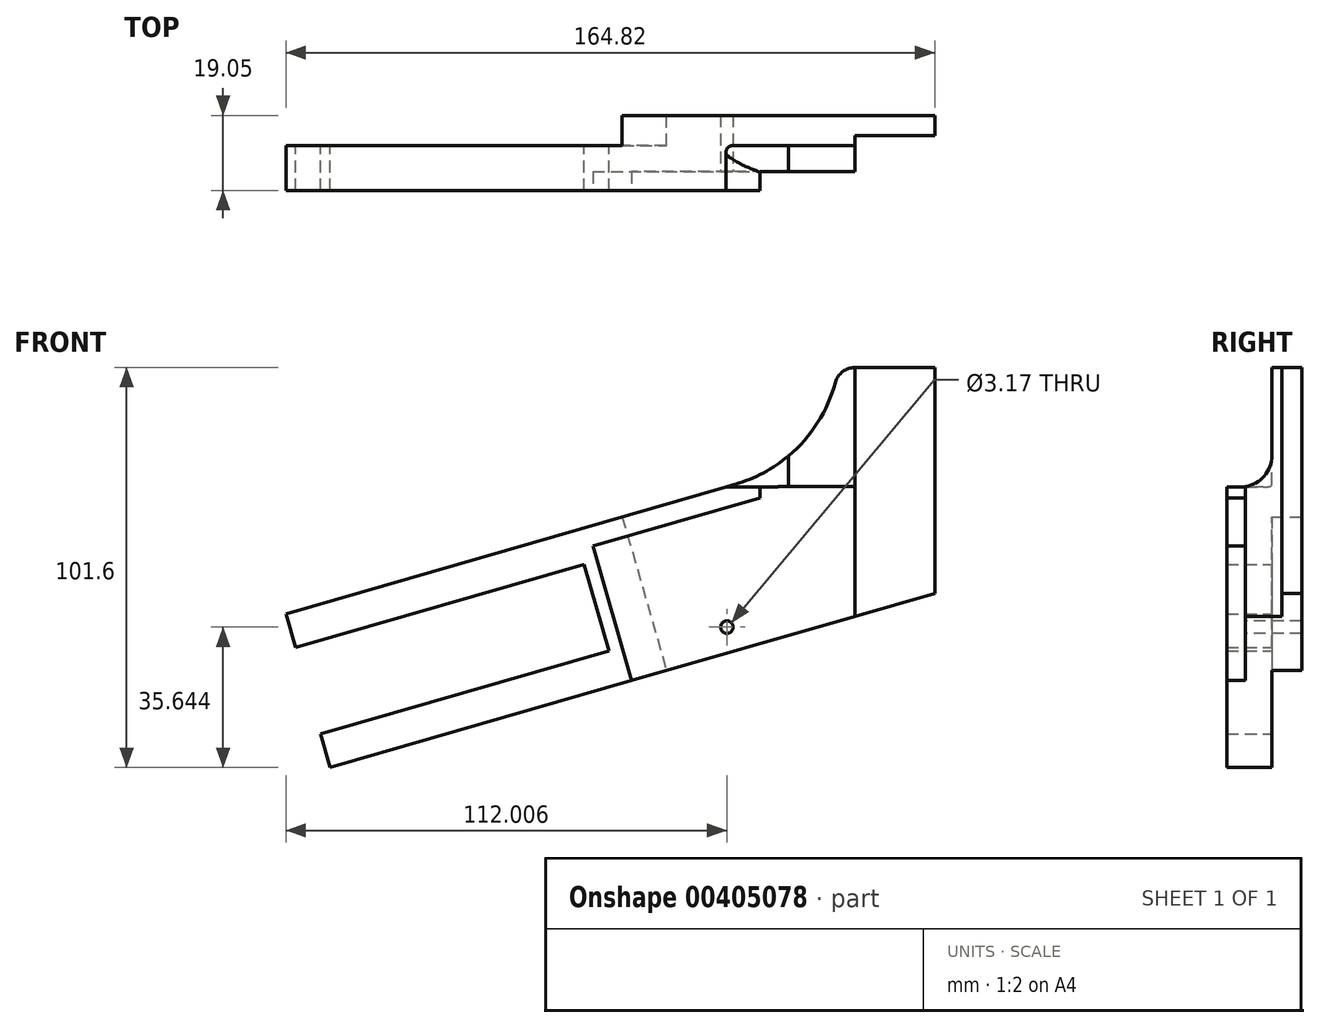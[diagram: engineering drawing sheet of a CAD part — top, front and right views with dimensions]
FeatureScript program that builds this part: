
annotation { "Feature Type Name" : "Feature", "Feature Type Description" : "" }
export const myFeature = defineFeature(function(context is Context, id is Id, definition is map)
    precondition{}
    {
        {
            var Q0;
            Q0=qCreatedBy(makeId("Front.planeOp"),FACE);
            var sketch = newSketch(context, id + "F0", { "sketchPlane" : qUnion([Q0])});
            skLineSegment(sketch, "E0.bottom", {"start": v(0, 0) * mm, "end": v(-50.8, 0) * mm});
            skLineSegment(sketch, "E0.top", {"start": v(0, -55.88) * mm, "end": v(-25.4, -55.88) * mm});
            skLineSegment(sketch, "E0.left", {"start": v(0, 0) * mm, "end": v(0, -55.88) * mm});
            skArc(sketch, "E1", {"start": v(-50.8, 0) * mm, "mid": v(-53.89, -1.05) * mm, "end": v(-55.7, -3.75) * mm});
            skLineSegment(sketch, "E2", {"start": v(-25.4, -55.88) * mm, "end": v(-184.04, -101.6) * mm});
            skLineSegment(sketch, "E3", {"start": v(-184.04, -101.6) * mm, "end": v(-186.5, -93.06) * mm});
            skLineSegment(sketch, "E4", {"start": v(-195.3, -62.55) * mm, "end": v(-81.19, -29.66) * mm});
            skArc(sketch, "E5", {"start": v(-81.19, -29.66) * mm, "mid": v(-65.05, -20.05) * mm, "end": v(-55.7, -3.75) * mm});
            skLineSegment(sketch, "E6", {"start": v(-192.84, -71.1) * mm, "end": v(-119.62, -50) * mm});
            skLineSegment(sketch, "E7", {"start": v(-119.62, -50) * mm, "end": v(-113.29, -71.96) * mm});
            skLineSegment(sketch, "E8", {"start": v(-113.29, -71.96) * mm, "end": v(-186.5, -93.06) * mm});
            skLineSegment(sketch, "E9.trimOffspring", {"start": v(-192.84, -71.1) * mm, "end": v(-195.3, -62.55) * mm});
            skLineSegment(sketch, "E10.bottom", {"start": v(-50.8, 0) * mm, "end": v(-30.48, 0) * mm});
            skLineSegment(sketch, "E10.left", {"start": v(-50.8, 0) * mm, "end": v(-50.8, -63.2) * mm});
            skLineSegment(sketch, "E10.right", {"start": v(-30.48, 0) * mm, "end": v(-30.48, -57.34) * mm});
            skSolve(sketch);
        }
        {
            var Q0;
            Q0=makeQuery(id+"F0.imprint","IMPRINT",FACE,{"disambiguationData":[TD([[makeQuery(id+"F0.imprint","IMPRINT",EDGE,{"derivedFrom":sQuery(id+"F0.wireOp",EDGE,"E0.bottom")}),1.0]])]});
            var Q1;
            Q1=makeQuery(id+"F0.imprint","IMPRINT",FACE,{"disambiguationData":[TD([[makeQuery(id+"F0.imprint","IMPRINT",EDGE,{"derivedFrom":sQuery(id+"F0.wireOp",EDGE,"E1")}),1.0]])]});
            var Q2;
            Q2=makeQuery(id+"F0.imprint","IMPRINT",FACE,{"disambiguationData":[TD([[makeQuery(id+"F0.imprint","IMPRINT",EDGE,{"derivedFrom":sQuery(id+"F0.wireOp",EDGE,"E10.bottom")}),-1.0]])]});
            extrude(context, id + "F1", {"entities" : qUnion([Q0, Q1, Q2]), "depth" : 19.05 * mm});
        }
        {
            var Q0;
            Q0=makeQuery(id+"F1.opExtrude","CAP_FACE",FACE,{"disambiguationData":[OSD([sQuery(id+"F0.wireOp",EDGE,"E0.bottom"),sQuery(id+"F0.wireOp",EDGE,"E0.top"),sQuery(id+"F0.wireOp",EDGE,"E0.left"),sQuery(id+"F0.wireOp",EDGE,"E1"),sQuery(id+"F0.wireOp",EDGE,"E2"),sQuery(id+"F0.wireOp",EDGE,"E3"),sQuery(id+"F0.wireOp",EDGE,"E4"),sQuery(id+"F0.wireOp",EDGE,"E5"),sQuery(id+"F0.wireOp",EDGE,"E6"),sQuery(id+"F0.wireOp",EDGE,"E7"),sQuery(id+"F0.wireOp",EDGE,"E8"),sQuery(id+"F0.wireOp",EDGE,"E9.trimOffspring"),sQuery(id+"F0.wireOp",EDGE,"E10.bottom")])],"isStart":false});
            var sketch = newSketch(context, id + "F2", { "sketchPlane" : qUnion([Q0])});
            skLineSegment(sketch, "E11.bottom", {"start": v(-50.8, 0) * mm, "end": v(-30.48, 0) * mm});
            skLineSegment(sketch, "E11.left", {"start": v(-50.8, 0) * mm, "end": v(-50.8, -63.2) * mm});
            skLineSegment(sketch, "E11.right", {"start": v(-30.48, 0) * mm, "end": v(-30.48, -57.34) * mm});
            skLineSegment(sketch, "E12", {"start": v(-30.48, -57.34) * mm, "end": v(-50.8, -63.2) * mm});
            skSolve(sketch);
        }
        {
            var Q0;
            Q0 = qSketchRegion(id + "F2", true);
            extrude(context, id + "F3", {"entities" : qUnion([Q0]), "operationType" : NewBodyOperationType.REMOVE, "oppositeDirection" : true, "depth" : 13.97 * mm});
        }
        {
            var Q0;
            Q0=makeQuery(id+"F0.imprint","IMPRINT",FACE,{"disambiguationData":[TD([[makeQuery(id+"F0.imprint","IMPRINT",EDGE,{"derivedFrom":sQuery(id+"F0.wireOp",EDGE,"E1")}),1.0]])]});
            var sketch = newSketch(context, id + "F4", { "sketchPlane" : qUnion([Q0])});
            skPoint(sketch, "E13", {"position": v(-195.3, -62.55) * mm});
            skPoint(sketch, "E14", {"position": v(-184.04, -101.6) * mm});
            skLineSegment(sketch, "E15", {"start": v(-195.3, -62.55) * mm, "end": v(-184.04, -101.6) * mm});
            skLineSegment(sketch, "E16", {"start": v(-184.04, -101.6) * mm, "end": v(-98.62, -76.98) * mm});
            skLineSegment(sketch, "E17", {"start": v(-195.3, -62.55) * mm, "end": v(-109.87, -37.93) * mm});
            skLineSegment(sketch, "E18", {"start": v(-109.87, -37.93) * mm, "end": v(-98.62, -76.98) * mm});
            skSolve(sketch);
        }
        {
            var Q0;
            Q0 = qSketchRegion(id + "F4", true);
            extrude(context, id + "F5", {"entities" : qUnion([Q0]), "operationType" : NewBodyOperationType.REMOVE, "depth" : 7.62 * mm});
        }
        {
            var Q0;
            {var subQ0=sQuery(id+"F0.wireOp",EDGE,"E2");var subQ1=sQuery(id+"F0.wireOp",EDGE,"E0.left");var subQ2=sQuery(id+"F0.wireOp",EDGE,"E0.top");var subQ3=sQuery(id+"F0.wireOp",EDGE,"E10.bottom");var subQ4=sQuery(id+"F0.wireOp",EDGE,"E0.bottom");Q0=makeQuery(id+"F3.boolean.opBoolean","SPLIT",FACE,{"disambiguationData":[TD([makeQuery(id+"F1.opExtrude","SWEPT_FACE",FACE,{"disambiguationData":[OSD([subQ2])]})])],"derivedFrom":makeQuery(id+"F1.opExtrude","CAP_FACE",FACE,{"disambiguationData":[OSD([subQ4,subQ2,subQ1,sQuery(id+"F0.wireOp",EDGE,"E1"),subQ0,sQuery(id+"F0.wireOp",EDGE,"E3"),sQuery(id+"F0.wireOp",EDGE,"E4"),sQuery(id+"F0.wireOp",EDGE,"E5"),sQuery(id+"F0.wireOp",EDGE,"E6"),sQuery(id+"F0.wireOp",EDGE,"E7"),sQuery(id+"F0.wireOp",EDGE,"E8"),sQuery(id+"F0.wireOp",EDGE,"E9.trimOffspring"),subQ3])],"isStart":false})});}
            var sketch = newSketch(context, id + "F6", { "sketchPlane" : qUnion([Q0])});
            skCircle(sketch, "E19", {"center": v(-6.35, -6.35) * mm, "radius": 3.18 * mm});
            skCircle(sketch, "E20", {"center": v(-24.13, -6.35) * mm, "radius": 3.18 * mm});
            skLineSegment(sketch, "E21", {"start": v(13.25, -21.59) * mm, "end": v(-85.18, -21.6) * mm, "construction": true});
            skPoint(sketch, "E22", {"position": v(-50.8, 0) * mm});
            skLineSegment(sketch, "E23", {"start": v(-50.8, -30.35) * mm, "end": v(-101.6, -30.35) * mm});
            skLineSegment(sketch, "E24", {"start": v(-50.8, 0) * mm, "end": v(-50.8, -30.35) * mm});
            skArc(sketch, "E25", {"start": v(-50.8, 0) * mm, "mid": v(-53.89, -1.05) * mm, "end": v(-55.7, -3.75) * mm});
            skArc(sketch, "E26", {"start": v(-101.6, -29.7) * mm, "mid": v(-73.23, -26.32) * mm, "end": v(-55.7, -3.75) * mm});
            skLineSegment(sketch, "E27", {"start": v(-101.6, -30.35) * mm, "end": v(-101.6, -29.7) * mm});
            skLineSegment(sketch, "E28", {"start": v(-30.48, -10.41) * mm, "end": v(-30.48, -32.77) * mm});
            skLineSegment(sketch, "E29", {"start": v(-30.48, -10.41) * mm, "end": v(-28.9, -10.41) * mm});
            skLineSegment(sketch, "E30", {"start": v(-28.9, -10.41) * mm, "end": v(-28.9, -32.77) * mm});
            skLineSegment(sketch, "E31", {"start": v(-28.9, -32.77) * mm, "end": v(-30.48, -32.77) * mm});
            skLineSegment(sketch, "E32", {"start": v(-28.9, -12.32) * mm, "end": v(-7.97, -12.32) * mm});
            skSolve(sketch);
        }
        {
            var Q0;
            {var subQ0=sQuery(id+"F6.wireOp",EDGE,"E24");Q0=makeQuery(id+"F6.imprint","IMPRINT",FACE,{"disambiguationData":[TD([[makeQuery(id+"F6.imprint","IMPRINT",EDGE,{"derivedFrom":subQ0}),-1.0]])]});}
            extrude(context, id + "F7", {"entities" : qUnion([Q0]), "operationType" : NewBodyOperationType.REMOVE, "oppositeDirection" : true, "depth" : 11.43 * mm});
        }
        {
            var Q0;
            Q0=makeQuery(id+"F7.boolean.opBoolean","COPY",EDGE,{"derivedFrom":makeQuery(id+"F7.opExtrude","CAP_EDGE",EDGE,{"disambiguationData":[OSD([sQuery(id+"F6.wireOp",EDGE,"E23")])],"isStart":false})});
            fillet(context, id + "F8", {"entities" : qUnion([Q0]), "radius" : 7.94 * mm, "tangentPropagation" : true, "allowEdgeOverflow" : false});
        }
        {
            var Q0;
            {var subQ0=sQuery(id+"F0.wireOp",EDGE,"E4");var subQ1=sQuery(id+"F0.wireOp",EDGE,"E3");var subQ2=sQuery(id+"F0.wireOp",EDGE,"E2");var subQ3=sQuery(id+"F0.wireOp",EDGE,"E1");var subQ4=sQuery(id+"F0.wireOp",EDGE,"E5");var subQ5=sQuery(id+"F0.wireOp",EDGE,"E6");var subQ6=sQuery(id+"F0.wireOp",EDGE,"E7");var subQ7=sQuery(id+"F0.wireOp",EDGE,"E8");var subQ8=sQuery(id+"F0.wireOp",EDGE,"E9.trimOffspring");Q0=makeQuery(id+"F3.boolean.opBoolean","SPLIT",FACE,{"disambiguationData":[TD([makeQuery(id+"F1.opExtrude","SWEPT_FACE",FACE,{"disambiguationData":[OSD([subQ3])]})])],"derivedFrom":makeQuery(id+"F1.opExtrude","CAP_FACE",FACE,{"disambiguationData":[OSD([sQuery(id+"F0.wireOp",EDGE,"E0.bottom"),sQuery(id+"F0.wireOp",EDGE,"E0.top"),sQuery(id+"F0.wireOp",EDGE,"E0.left"),subQ3,subQ2,subQ1,subQ0,subQ4,subQ5,subQ6,subQ7,subQ8,sQuery(id+"F0.wireOp",EDGE,"E10.bottom")])],"isStart":false})});}
            var sketch = newSketch(context, id + "F9", { "sketchPlane" : qUnion([Q0])});
            skLineSegment(sketch, "E33", {"start": v(22.55, -19.05) * mm, "end": v(-137.17, -19.05) * mm, "construction": true});
            skLineSegment(sketch, "E34", {"start": v(-216.65, -89.85) * mm, "end": v(44.78, -14.5) * mm, "construction": true});
            skLineSegment(sketch, "E35", {"start": v(-40.64, 0) * mm, "end": v(-40.64, -73.86) * mm, "construction": true});
            skCircle(sketch, "E36", {"center": v(-40.64, -50.8) * mm, "radius": 38.1 * mm});
            skCircle(sketch, "E37", {"center": v(-40.64, -50.8) * mm, "radius": 4.76 * mm});
            skCircle(sketch, "E38", {"center": v(-40.64, -50.8) * mm, "radius": 3.18 * mm});
            skLineSegment(sketch, "E39.top", {"start": v(-53.98, -22.23) * mm, "end": v(-53.98, -22.23) * mm});
            skCircle(sketch, "E40", {"center": v(-73.37, -44.45) * mm, "radius": 4.76 * mm});
            skLineSegment(sketch, "E41", {"start": v(-74.91, -49) * mm, "end": v(-41.55, -55.48) * mm});
            skLineSegment(sketch, "E42", {"start": v(-53.98, -22.23) * mm, "end": v(-53.98, -14.4) * mm});
            skLineSegment(sketch, "E43", {"start": v(-53.98, -14.4) * mm, "end": v(-68.58, -3.18) * mm});
            skLineSegment(sketch, "E44", {"start": v(-68.58, -3.18) * mm, "end": v(-60.07, -18.02) * mm});
            skCircle(sketch, "E45", {"center": v(-40.64, -30.4) * mm, "radius": 15.64 * mm});
            skLineSegment(sketch, "E46", {"start": v(-94.35, -75.75) * mm, "end": v(-78.48, -71.18) * mm});
            skLineSegment(sketch, "E47", {"start": v(-78.48, -71.18) * mm, "end": v(-81.12, -62.03) * mm});
            skLineSegment(sketch, "E48", {"start": v(-81.12, -62.03) * mm, "end": v(-96.99, -66.6) * mm});
            skLineSegment(sketch, "E49", {"start": v(-96.99, -66.6) * mm, "end": v(-94.35, -75.75) * mm});
            skLineSegment(sketch, "E50", {"start": v(-86.42, -73.46) * mm, "end": v(-80.09, -95.43) * mm});
            skLineSegment(sketch, "E51", {"start": v(-80.09, -95.43) * mm, "end": v(-94.35, -75.75) * mm});
            skCircle(sketch, "E52", {"center": v(-83.3, -65.96) * mm, "radius": 1.59 * mm});
            skLineSegment(sketch, "E53", {"start": v(-65.92, -60.95) * mm, "end": v(-107.75, -73) * mm, "construction": true});
            skPoint(sketch, "E54", {"position": v(-195.3, -62.55) * mm});
            skPoint(sketch, "E55", {"position": v(-192.84, -71.1) * mm});
            skCircle(sketch, "E56", {"center": v(-93.06, -68.77) * mm, "radius": 1.59 * mm});
            skLineSegment(sketch, "E57", {"start": v(-78.13, -19.05) * mm, "end": v(-78.13, -106.08) * mm, "construction": true});
            skLineSegment(sketch, "E58", {"start": v(-117.33, -45.37) * mm, "end": v(-84.15, -35.8) * mm});
            skLineSegment(sketch, "E59", {"start": v(-84.15, -35.8) * mm, "end": v(-61.15, -29.18) * mm});
            skLineSegment(sketch, "E60", {"start": v(-117.33, -45.37) * mm, "end": v(-107.48, -79.54) * mm});
            skLineSegment(sketch, "E61", {"start": v(-107.48, -79.54) * mm, "end": v(-50.8, -63.2) * mm});
            skLineSegment(sketch, "E62", {"start": v(-74.93, -33.15) * mm, "end": v(-74.93, -28.4) * mm});
            skLineSegment(sketch, "E63", {"start": v(-74.93, -28.4) * mm, "end": v(-49.66, -28.4) * mm});
            skLineSegment(sketch, "E64", {"start": v(-50.8, -63.2) * mm, "end": v(-50.8, -28.4) * mm});
            skSolve(sketch);
        }
        {
            var Q0;
            {var subQ6=sQuery(id+"F9.wireOp",EDGE,"E47");Q0=makeQuery(id+"F9.imprint","IMPRINT",FACE,{"disambiguationData":[TD([[makeQuery(id+"F9.imprint","IMPRINT",EDGE,{"derivedFrom":subQ6}),-1.0]])]});}
            var Q1;
            {var subQ1=sQuery(id+"F9.wireOp",EDGE,"E47");Q1=makeQuery(id+"F9.imprint","IMPRINT",FACE,{"disambiguationData":[TD([[makeQuery(id+"F9.imprint","IMPRINT",EDGE,{"derivedFrom":subQ1}),1.0]])]});}
            var Q2;
            Q2=makeQuery(id+"F9.imprint","IMPRINT",FACE,{"disambiguationData":[TD([[makeQuery(id+"F9.imprint","IMPRINT",EDGE,{"derivedFrom":sQuery(id+"F9.wireOp",EDGE,"E52")}),1.0]])]});
            var Q3;
            Q3=makeQuery(id+"F9.imprint","IMPRINT",FACE,{"disambiguationData":[TD([[makeQuery(id+"F9.imprint","IMPRINT",EDGE,{"derivedFrom":sQuery(id+"F9.wireOp",EDGE,"E56")}),1.0]])]});
            var Q4;
            {var subQ1=sQuery(id+"F9.wireOp",EDGE,"E61");var subQ3=sQuery(id+"F9.wireOp",EDGE,"E36");var subQ4=makeQuery(id+"F9.imprint","INTERSECT",VERTEX,{"derivedFrom":[subQ3,subQ1]});Q4=makeQuery(id+"F9.imprint","IMPRINT",FACE,{"disambiguationData":[TD([[makeQuery(id+"F9.imprint","IMPRINT",EDGE,{"disambiguationData":[TD([[subQ4,1.0]])],"derivedFrom":subQ3}),1.0]])]});}
            var Q5;
            {var subQ5=sQuery(id+"F9.wireOp",EDGE,"E36");var subQ11=sQuery(id+"F9.wireOp",EDGE,"E59");var subQ12=makeQuery(id+"F9.imprint","INTERSECT",VERTEX,{"derivedFrom":[subQ5,subQ11]});Q5=makeQuery(id+"F9.imprint","IMPRINT",FACE,{"disambiguationData":[TD([[makeQuery(id+"F9.imprint","IMPRINT",EDGE,{"disambiguationData":[TD([[subQ12,-1.0]])],"derivedFrom":subQ5}),1.0]])]});}
            var Q6;
            {var subQ0=sQuery(id+"F9.wireOp",EDGE,"E40");var subQ1=makeQuery(id+"F9.imprint","INTERSECT",VERTEX,{"derivedFrom":[subQ0,sQuery(id+"F9.wireOp",EDGE,"E41")]});Q6=makeQuery(id+"F9.imprint","IMPRINT",FACE,{"disambiguationData":[TD([[makeQuery(id+"F9.imprint","IMPRINT",EDGE,{"disambiguationData":[TD([[subQ1,1.0]])],"derivedFrom":subQ0}),1.0]])]});}
            var Q7;
            {var subQ5=sQuery(id+"F9.wireOp",EDGE,"kIZxa004-UBnl-Zp0g-NPGq-y5hxtPQhJK6m");Q7=makeQuery(id+"F9.imprint","IMPRINT",FACE,{"disambiguationData":[TD([[makeQuery(id+"F9.imprint","IMPRINT",EDGE,{"derivedFrom":subQ5}),1.0]])]});}
            var Q8;
            {var subQ0=sQuery(id+"F9.wireOp",EDGE,"E64");var subQ1=sQuery(id+"F9.wireOp",EDGE,"E45");var subQ2=makeQuery(id+"F9.imprint","INTERSECT",VERTEX,{"derivedFrom":[subQ1,subQ0]});Q8=makeQuery(id+"F9.imprint","IMPRINT",FACE,{"disambiguationData":[TD([[makeQuery(id+"F9.imprint","IMPRINT",EDGE,{"disambiguationData":[TD([[subQ2,1.0]])],"derivedFrom":subQ1}),1.0]])]});}
            var Q9;
            {var subQ0=sQuery(id+"F9.wireOp",EDGE,"E63");var subQ1=sQuery(id+"F9.wireOp",EDGE,"E45");var subQ2=makeQuery(id+"F9.imprint","INTERSECT",VERTEX,{"derivedFrom":[subQ1,subQ0]});Q9=makeQuery(id+"F9.imprint","IMPRINT",FACE,{"disambiguationData":[TD([[makeQuery(id+"F9.imprint","IMPRINT",EDGE,{"disambiguationData":[TD([[subQ2,-1.0]])],"derivedFrom":subQ1}),1.0]])]});}
            var Q10;
            {var subQ2=sQuery(id+"F9.wireOp",EDGE,"E36");var subQ4=sQuery(id+"F9.wireOp",EDGE,"E63");var subQ5=makeQuery(id+"F9.imprint","INTERSECT",VERTEX,{"derivedFrom":[subQ2,subQ4]});Q10=makeQuery(id+"F9.imprint","IMPRINT",FACE,{"disambiguationData":[TD([[makeQuery(id+"F9.imprint","IMPRINT",EDGE,{"disambiguationData":[TD([[subQ5,-1.0]])],"derivedFrom":subQ2}),1.0]])]});}
            var Q11;
            {var subQ0=sQuery(id+"F9.wireOp",EDGE,"E63");var subQ1=sQuery(id+"F9.wireOp",EDGE,"E36");var subQ2=makeQuery(id+"F9.imprint","INTERSECT",VERTEX,{"derivedFrom":[subQ1,subQ0]});Q11=makeQuery(id+"F9.imprint","IMPRINT",FACE,{"disambiguationData":[TD([[makeQuery(id+"F9.imprint","IMPRINT",EDGE,{"disambiguationData":[TD([[subQ2,-1.0]])],"derivedFrom":subQ1}),-1.0]])]});}
            var Q12;
            {var subQ0=sQuery(id+"F9.wireOp",EDGE,"E59");var subQ1=sQuery(id+"F9.wireOp",EDGE,"E36");var subQ2=makeQuery(id+"F9.imprint","INTERSECT",VERTEX,{"derivedFrom":[subQ1,subQ0]});Q12=makeQuery(id+"F9.imprint","IMPRINT",FACE,{"disambiguationData":[TD([[makeQuery(id+"F9.imprint","IMPRINT",EDGE,{"disambiguationData":[TD([[subQ2,1.0]])],"derivedFrom":subQ1}),1.0]])]});}
            var Q13;
            {var subQ0=sQuery(id+"F9.wireOp",EDGE,"E59");var subQ1=sQuery(id+"F9.wireOp",EDGE,"E36");var subQ2=makeQuery(id+"F9.imprint","INTERSECT",VERTEX,{"derivedFrom":[subQ1,subQ0]});Q13=makeQuery(id+"F9.imprint","IMPRINT",FACE,{"disambiguationData":[TD([[makeQuery(id+"F9.imprint","IMPRINT",EDGE,{"disambiguationData":[TD([[subQ2,1.0]])],"derivedFrom":subQ1}),-1.0]])]});}
            extrude(context, id + "F10", {"entities" : qUnion([Q0, Q1, Q2, Q3, Q4, Q5, Q6, Q7, Q8, Q9, Q10, Q11, Q12, Q13]), "operationType" : NewBodyOperationType.REMOVE, "oppositeDirection" : true, "depth" : 4.76 * mm, "offsetDistance" : 25.4 * mm});
        }
        {
            var Q0;
            Q0=makeQuery(id+"F9.imprint","IMPRINT",FACE,{"disambiguationData":[TD([[makeQuery(id+"F9.imprint","IMPRINT",EDGE,{"derivedFrom":sQuery(id+"F9.wireOp",EDGE,"E52")}),1.0]])]});
            extrude(context, id + "F11", {"entities" : qUnion([Q0]), "operationType" : NewBodyOperationType.REMOVE, "endBound" : BoundingType.THROUGH_ALL, "oppositeDirection" : true, "depth" : 25.4 * mm, "offsetDistance" : 25.4 * mm});
        }
    });
